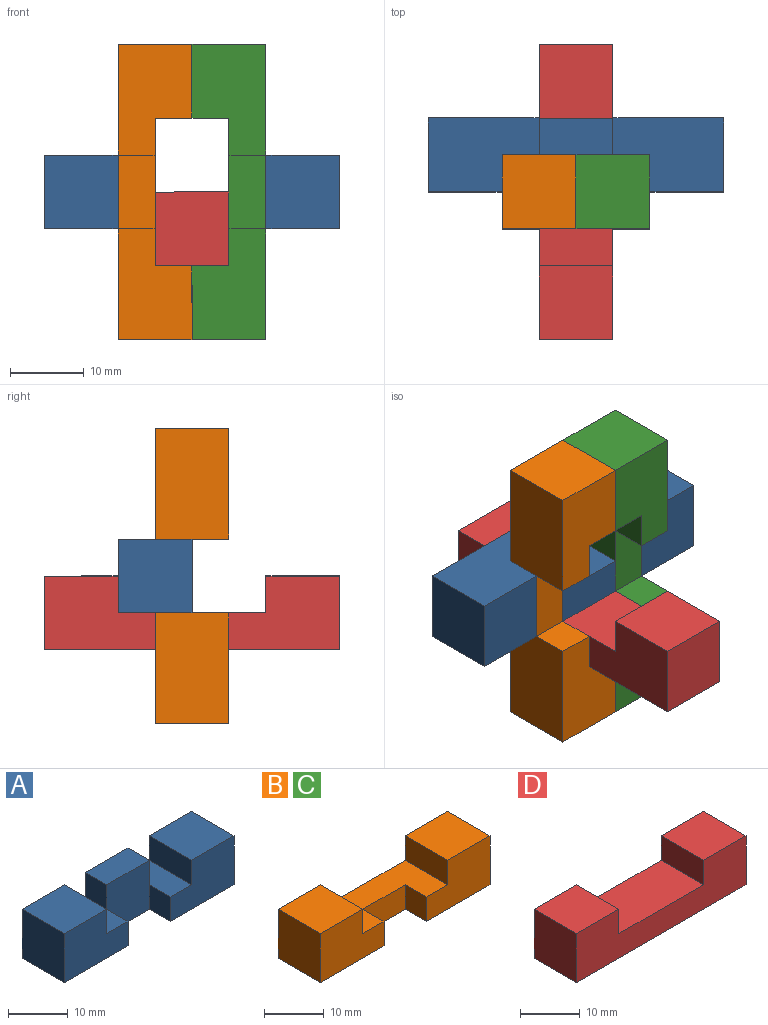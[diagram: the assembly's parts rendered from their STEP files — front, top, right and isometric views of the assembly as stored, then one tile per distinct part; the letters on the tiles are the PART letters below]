
ASSEMBLY  parts=4 mates=3
PART A: 18 faces, bbox 40x10x10 mm
  f0: plane 10x5mm, normal (0,0,1), area 50mm2, adj f1,f5,f11,f12,f16
  f1: plane 15x10mm, normal (0,-1,0), area 125mm2, adj f0,f2,f4,f7,f11,f12
  f2: plane 40x10mm, normal (0,0,-1), area 350mm2, adj f1,f3,f5,f6,f7,f12,f13,f14
  f3: plane 15x10mm, normal (0,-1,0), area 125mm2, adj f2,f6,f8,f9,f10,f13
  f4: plane 10x10mm, normal (0,0,1), area 100mm2, adj f1,f5,f7,f11
  f5: plane 40x10mm, normal (0,1,0), area 350mm2, adj f0,f2,f4,f6,f7,f8,f9,f10
  f6: plane 10x10mm, normal (-1,0,0), area 100mm2, adj f2,f3,f5,f8
  f7: plane 10x10mm, normal (1,0,0), area 100mm2, adj f1,f2,f4,f5
  f8: plane 10x10mm, normal (0,0,1), area 100mm2, adj f3,f5,f6,f9
  f9: plane 10x5mm, normal (1,0,0), area 50mm2, adj f3,f5,f8,f10
  f10: plane 10x5mm, normal (0,0,1), area 50mm2, adj f3,f5,f9,f13,f15
  f11: plane 10x5mm, normal (-1,0,0), area 50mm2, adj f0,f1,f4,f5
  f12: plane 5x5mm, normal (-1,0,0), area 25mm2, adj f0,f1,f2,f14
  f13: plane 5x5mm, normal (1,0,0), area 25mm2, adj f2,f3,f10,f14
  f14: plane 10x10mm, normal (0,-1,0), area 100mm2, adj f2,f12,f13,f15,f16,f17
  f15: plane 5x5mm, normal (-1,0,0), area 25mm2, adj f5,f10,f14,f17
  f16: plane 5x5mm, normal (1,0,0), area 25mm2, adj f0,f5,f14,f17
  f17: plane 10x5mm, normal (0,0,1), area 50mm2, adj f5,f14,f15,f16
PART B: 14 faces, bbox 40x10x10 mm
  f0: plane 15x10mm, normal (0,-1,0), area 125mm2, adj f1,f3,f6,f9,f10,f11
  f1: plane 40x10mm, normal (0,0,-1), area 350mm2, adj f0,f2,f4,f5,f6,f11,f12,f13
  f2: plane 15x10mm, normal (0,-1,0), area 125mm2, adj f1,f5,f7,f8,f9,f12
  f3: plane 10x10mm, normal (0,0,1), area 100mm2, adj f0,f4,f6,f10
  f4: plane 40x10mm, normal (0,1,0), area 300mm2, adj f1,f3,f5,f6,f7,f8,f9,f10
  f5: plane 10x10mm, normal (-1,0,0), area 100mm2, adj f1,f2,f4,f7
  f6: plane 10x10mm, normal (1,0,0), area 100mm2, adj f0,f1,f3,f4
  f7: plane 10x10mm, normal (0,0,1), area 100mm2, adj f2,f4,f5,f8
  f8: plane 10x5mm, normal (1,0,0), area 50mm2, adj f2,f4,f7,f9
  f9: plane 20x10mm, normal (0,0,1), area 150mm2, adj f0,f2,f4,f8,f10,f11,f12,f13
  f10: plane 10x5mm, normal (-1,0,0), area 50mm2, adj f0,f3,f4,f9
  f11: plane 5x5mm, normal (-1,0,0), area 25mm2, adj f0,f1,f9,f13
  f12: plane 5x5mm, normal (1,0,0), area 25mm2, adj f1,f2,f9,f13
  f13: plane 10x5mm, normal (0,-1,0), area 50mm2, adj f1,f9,f11,f12
PART C: same geometry as B
PART D: 10 faces, bbox 40x10x10 mm
  f0: plane 40x10mm, normal (0,-1,0), area 300mm2, adj f1,f3,f4,f5,f6,f7,f8,f9
  f1: plane 10x10mm, normal (0,0,1), area 100mm2, adj f0,f2,f4,f9
  f2: plane 40x10mm, normal (0,1,0), area 300mm2, adj f1,f3,f4,f5,f6,f7,f8,f9
  f3: plane 10x10mm, normal (-1,0,0), area 100mm2, adj f0,f2,f5,f6
  f4: plane 10x10mm, normal (1,0,0), area 100mm2, adj f0,f1,f2,f6
  f5: plane 10x10mm, normal (0,0,1), area 100mm2, adj f0,f2,f3,f7
  f6: plane 40x10mm, normal (0,0,-1), area 400mm2, adj f0,f2,f3,f4
  f7: plane 10x5mm, normal (1,0,0), area 50mm2, adj f0,f2,f5,f8
  f8: plane 20x10mm, normal (0,0,1), area 200mm2, adj f0,f2,f7,f9
  f9: plane 10x5mm, normal (-1,0,0), area 50mm2, adj f0,f1,f2,f8
PLACE A rot(axis=(0,-0.71,0.71),180deg) t=(-5,30,-10)mm
PLACE B rot(axis=(0,1,0),90deg) t=(-15,20,-10)mm
PLACE C rot(axis=(0,-1,0),90deg) t=(5,20,-10)mm fixed
PLACE D rot(axis=(0,0,1),90deg) t=(-5,20,-20)mm
MATE slider B.f4 <-> D.f3  axis (0,1,0) through (-5,25,-20)mm
MATE fastened B.f7 <-> C.f3  axis (1,0,0) through (-5,20,5)mm
MATE fastened A.f2 <-> D.f9  axis (0,1,0) through (-5,30,-10)mm
